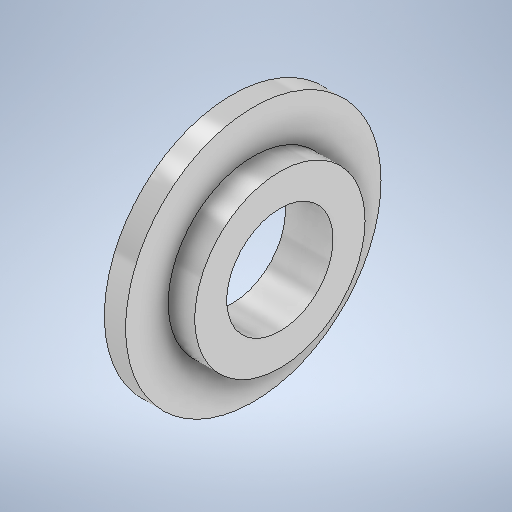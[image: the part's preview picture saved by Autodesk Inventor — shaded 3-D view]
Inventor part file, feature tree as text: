
AUTODESK INVENTOR PART (.ipt)
format: ipt  version: 2025.1 (Build 291241000, 241)  size: 270,848 bytes
history: native  units: mm
features: sketch x2, revolve x1, hole x1
ambient origin geometry x8: Origin, YZ Plane, XZ Plane, XY Plane, X Axis, Y Axis, Z Axis, Center Point
bodies: Solid1 (feature_tree)
feature tree (4):
  revolve  "Revolution1"  [1 undecoded]
  hole  "Hole1"  [1 undecoded]
  sketch  "Sketch1"  dims[d0=2.5mm d1=2.0mm]
  sketch  "Sketch2"  dims[d2=24.0mm d3=16.0mm d4=90.0deg d5=10.0mm d6=10.0mm d7=4.0mm d8=2.0mm d9=90.0deg d10=8.0mm d11=0.0mm]
note: 2 required parameter values undecoded (feature->parameter linkage not recoverable at this tier; creation-order binding heuristic only, values carry confidence <= 0.55)